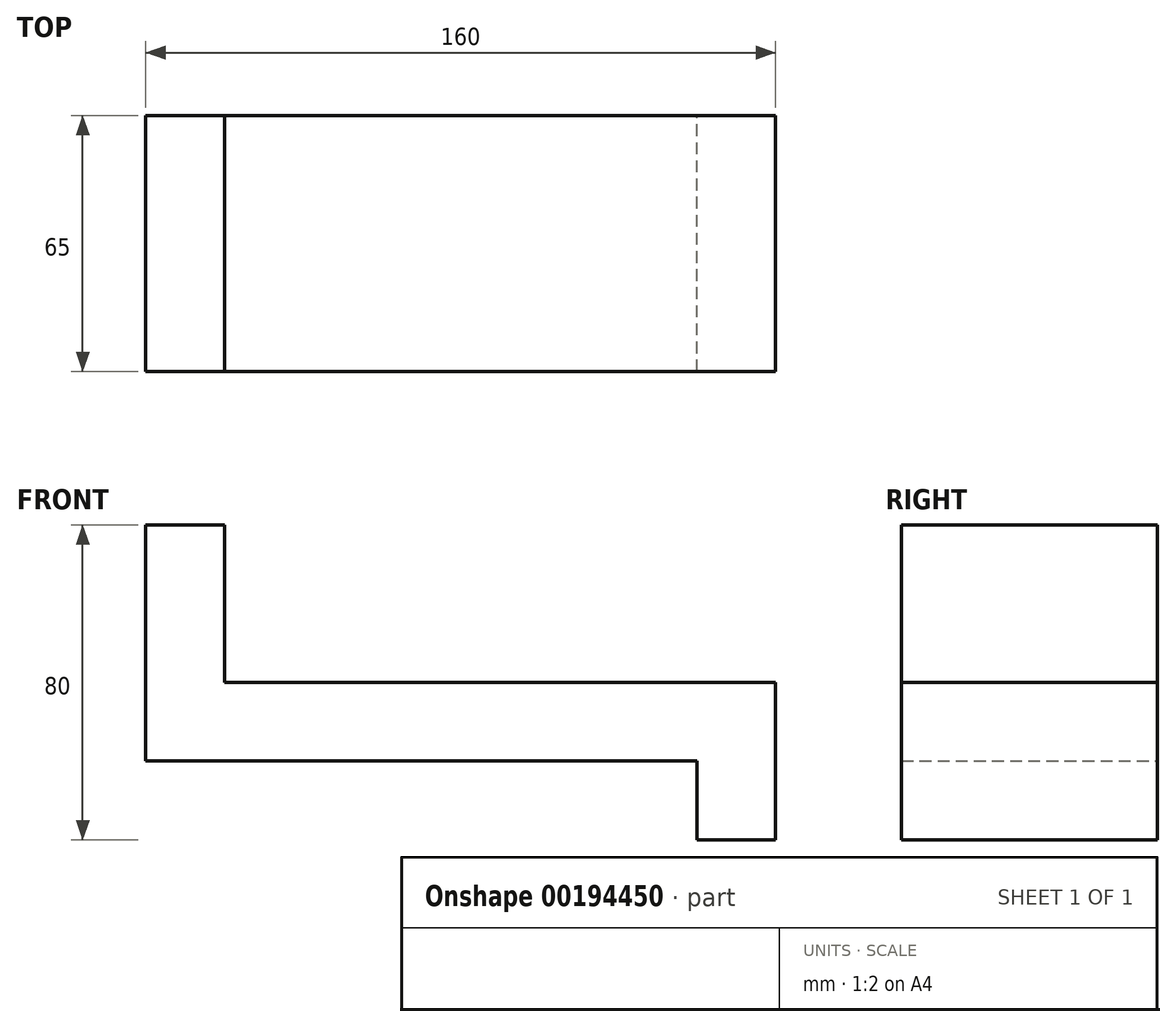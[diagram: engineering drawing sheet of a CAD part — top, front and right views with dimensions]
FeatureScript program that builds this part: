
annotation { "Feature Type Name" : "Feature", "Feature Type Description" : "" }
export const myFeature = defineFeature(function(context is Context, id is Id, definition is map)
    precondition{}
    {
        {
            var Q0;
            Q0=qCreatedBy(makeId("Front.planeOp"),FACE);
            var sketch = newSketch(context, id + "F0", { "sketchPlane" : qUnion([Q0])});
            skLineSegment(sketch, "E0", {"start": v(0, 60) * mm, "end": v(0, 0) * mm});
            skLineSegment(sketch, "E1", {"start": v(0, 0) * mm, "end": v(140, 0) * mm});
            skLineSegment(sketch, "E2", {"start": v(140, 0) * mm, "end": v(140, -20) * mm});
            skLineSegment(sketch, "E3", {"start": v(140, -20) * mm, "end": v(160, -20) * mm});
            skLineSegment(sketch, "E4", {"start": v(160, -20) * mm, "end": v(160, 20) * mm});
            skLineSegment(sketch, "E5", {"start": v(160, 20) * mm, "end": v(20, 20) * mm});
            skLineSegment(sketch, "E6", {"start": v(20, 20) * mm, "end": v(20, 60) * mm});
            skLineSegment(sketch, "E7", {"start": v(20, 60) * mm, "end": v(0, 60) * mm});
            skSolve(sketch);
        }
        {
            var Q0;
            Q0 = qSketchRegion(id + "F0", true);
            extrude(context, id + "F1", {"entities" : qUnion([Q0]), "depth" : 65 * mm});
        }
    });
